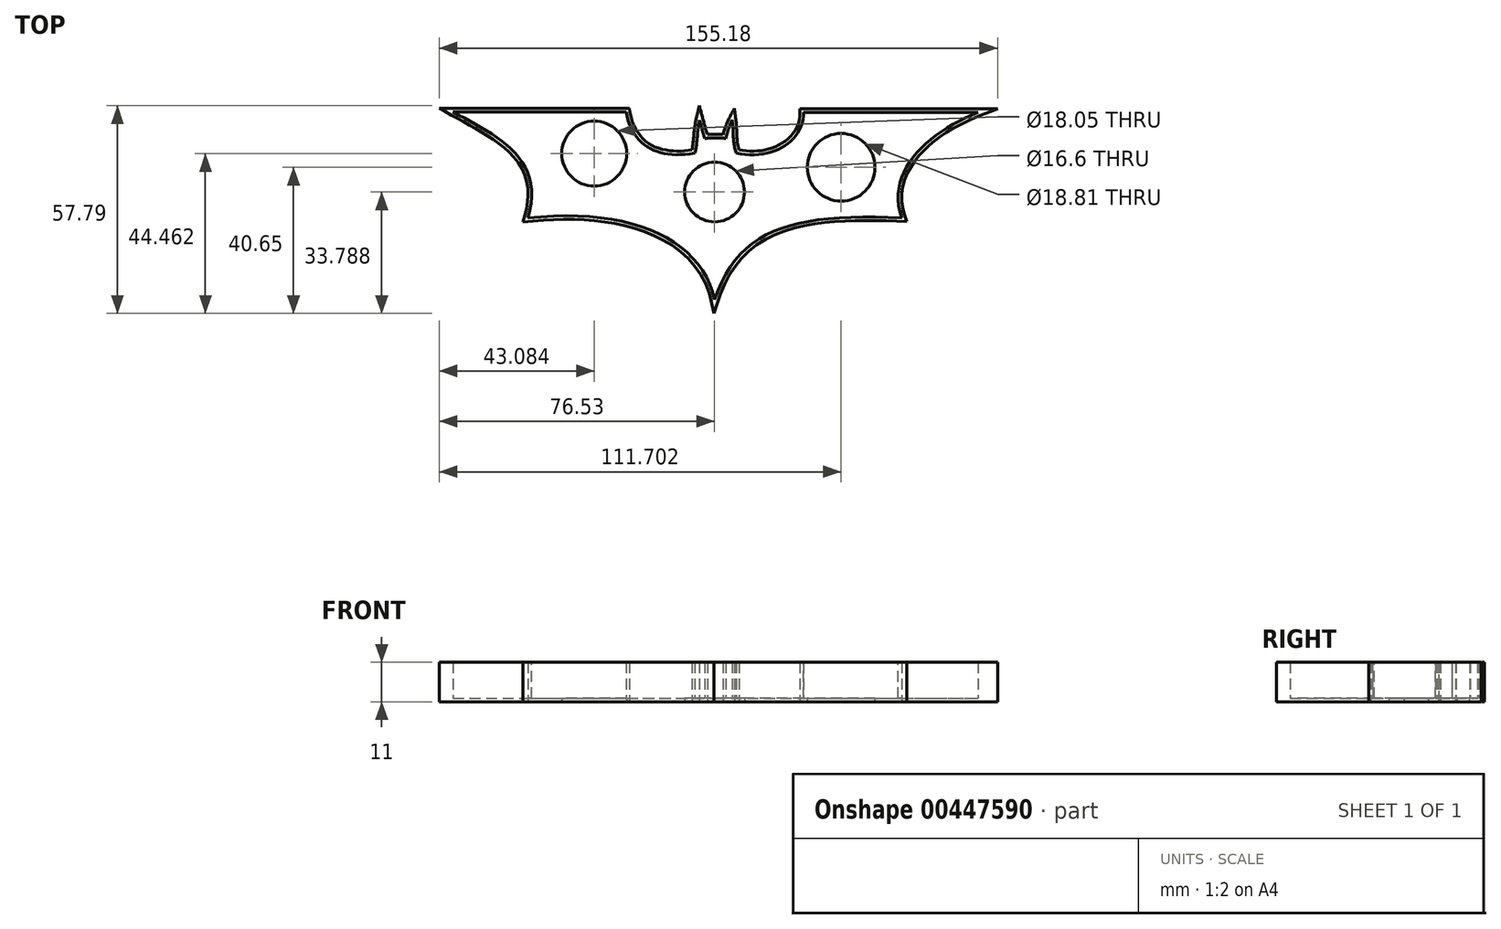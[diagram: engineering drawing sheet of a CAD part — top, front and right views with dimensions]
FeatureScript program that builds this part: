
annotation { "Feature Type Name" : "Feature", "Feature Type Description" : "" }
export const myFeature = defineFeature(function(context is Context, id is Id, definition is map)
    precondition{}
    {
        {
            var Q0;
            Q0=qCreatedBy(makeId("Top.planeOp"),FACE);
            var sketch = newSketch(context, id + "F0", { "sketchPlane" : qUnion([Q0])});
            skLineSegment(sketch, "E0", {"start": v(-72.67, 53.69) * mm, "end": v(-24.57, 53.69) * mm});
            skLineSegment(sketch, "E1", {"start": v(24.76, 53.53) * mm, "end": v(73.3, 53.53) * mm});
            skFitSpline(sketch, "E2", {"points": [v(-72.67, 53.69) * mm, v(-51.88, 24.18) * mm], "startDerivative": vector(35.2, -19.56) * mm, "endDerivative": vector(-15.13, -50.45) * mm});
            skFitSpline(sketch, "E3", {"points": [v(-51.88, 24.18) * mm, v(0, 1.44) * mm], "startDerivative": vector(84.4, 9.38) * mm, "endDerivative": vector(11.12, -51.36) * mm});
            skFitSpline(sketch, "E4", {"points": [v(0, 1.44) * mm, v(52, 24.25) * mm], "startDerivative": vector(20.1, 60.81) * mm, "endDerivative": vector(88.06, -3.81) * mm});
            skFitSpline(sketch, "E5", {"points": [v(52, 24.25) * mm, v(73.3, 53.53) * mm], "startDerivative": vector(-13.74, 39.14) * mm, "endDerivative": vector(41.73, 16.14) * mm});
            skFitSpline(sketch, "E6", {"points": [v(24.76, 53.53) * mm, v(6.02, 42.26) * mm], "startDerivative": vector(0.1, -24.42) * mm, "endDerivative": vector(-29.53, 6.62) * mm});
            skFitSpline(sketch, "E7", {"points": [v(6.02, 42.26) * mm, v(4.92, 51.46) * mm], "startDerivative": vector(-3.31, 8.83) * mm, "endDerivative": vector(-1.1, 8.92) * mm});
            skFitSpline(sketch, "E8", {"points": [v(4.92, 51.46) * mm, v(3.17, 46.3) * mm], "startDerivative": vector(-2.48, -4.7) * mm, "endDerivative": vector(-0.83, -4.7) * mm});
            skFitSpline(sketch, "E9", {"points": [v(3.17, 46.3) * mm, v(-2.72, 46.3) * mm], "startDerivative": vector(-5.52, 0.55) * mm, "endDerivative": vector(-5.8, -0.83) * mm});
            skFitSpline(sketch, "E10", {"points": [v(-2.72, 46.3) * mm, v(-4.19, 51.37) * mm], "startDerivative": vector(-1.66, 4.97) * mm, "endDerivative": vector(-1.66, 6.07) * mm});
            skFitSpline(sketch, "E11", {"points": [v(-4.19, 51.37) * mm, v(-5.5, 42.24) * mm], "startDerivative": vector(-2.2, -9.38) * mm, "endDerivative": vector(-2.42, -8.07) * mm});
            skFitSpline(sketch, "E12", {"points": [v(-24.57, 53.69) * mm, v(-5.5, 42.24) * mm], "startDerivative": vector(5.16, -28.3) * mm, "endDerivative": vector(31.43, 5.47) * mm});
            skSolve(sketch);
        }
        {
            var Q0;
            Q0 = qSketchRegion(id + "F0", true);
            extrude(context, id + "F1", {"entities" : qUnion([Q0]), "depth" : 10 * mm});
        }
        {
            var Q0;
            Q0=makeQuery(id+"F1.opExtrude","CAP_FACE",FACE,{"disambiguationData":[OSD([sQuery(id+"F0.wireOp",EDGE,"E0"),sQuery(id+"F0.wireOp",EDGE,"E1"),sQuery(id+"F0.wireOp",EDGE,"E2"),sQuery(id+"F0.wireOp",EDGE,"E3"),sQuery(id+"F0.wireOp",EDGE,"E4"),sQuery(id+"F0.wireOp",EDGE,"E5"),sQuery(id+"F0.wireOp",EDGE,"E6"),sQuery(id+"F0.wireOp",EDGE,"E7"),sQuery(id+"F0.wireOp",EDGE,"E8"),sQuery(id+"F0.wireOp",EDGE,"E9"),sQuery(id+"F0.wireOp",EDGE,"E10"),sQuery(id+"F0.wireOp",EDGE,"E11"),sQuery(id+"F0.wireOp",EDGE,"E12")])],"isStart":false});
            shell(context, id + "F2", {"entities" : qUnion([Q0]), "thickness" : 1 * mm, "oppositeDirection" : true});
        }
        {
            var Q0;
            Q0=makeQuery(id+"F1.opExtrude","CAP_FACE",FACE,{"disambiguationData":[OSD([sQuery(id+"F0.wireOp",EDGE,"E0"),sQuery(id+"F0.wireOp",EDGE,"E1"),sQuery(id+"F0.wireOp",EDGE,"E2"),sQuery(id+"F0.wireOp",EDGE,"E3"),sQuery(id+"F0.wireOp",EDGE,"E4"),sQuery(id+"F0.wireOp",EDGE,"E5"),sQuery(id+"F0.wireOp",EDGE,"E6"),sQuery(id+"F0.wireOp",EDGE,"E7"),sQuery(id+"F0.wireOp",EDGE,"E8"),sQuery(id+"F0.wireOp",EDGE,"E9"),sQuery(id+"F0.wireOp",EDGE,"E10"),sQuery(id+"F0.wireOp",EDGE,"E11"),sQuery(id+"F0.wireOp",EDGE,"E12")])],"isStart":true});
            var sketch = newSketch(context, id + "F3", { "sketchPlane" : qUnion([Q0])});
            skCircle(sketch, "E13", {"center": v(35.17, -38.3) * mm, "radius": 9.4 * mm});
            skCircle(sketch, "E14", {"center": v(-33.45, -42.1) * mm, "radius": 9.02 * mm});
            skCircle(sketch, "E15", {"center": v(0, -31.43) * mm, "radius": 8.3 * mm});
            skSolve(sketch);
        }
        {
            var Q0;
            Q0=makeQuery(id+"F3.imprint","IMPRINT",FACE,{"disambiguationData":[TD([[makeQuery(id+"F3.imprint","IMPRINT",EDGE,{"derivedFrom":sQuery(id+"F3.wireOp",EDGE,"E13")}),1.0]])]});
            var Q1;
            Q1=makeQuery(id+"F3.imprint","IMPRINT",FACE,{"disambiguationData":[TD([[makeQuery(id+"F3.imprint","IMPRINT",EDGE,{"derivedFrom":sQuery(id+"F3.wireOp",EDGE,"E15")}),1.0]])]});
            var Q2;
            Q2=makeQuery(id+"F3.imprint","IMPRINT",FACE,{"disambiguationData":[TD([[makeQuery(id+"F3.imprint","IMPRINT",EDGE,{"derivedFrom":sQuery(id+"F3.wireOp",EDGE,"E14")}),1.0]])]});
            extrude(context, id + "F4", {"entities" : qUnion([Q0, Q1, Q2]), "operationType" : NewBodyOperationType.REMOVE, "oppositeDirection" : true, "depth" : 25 * mm});
        }
    });
